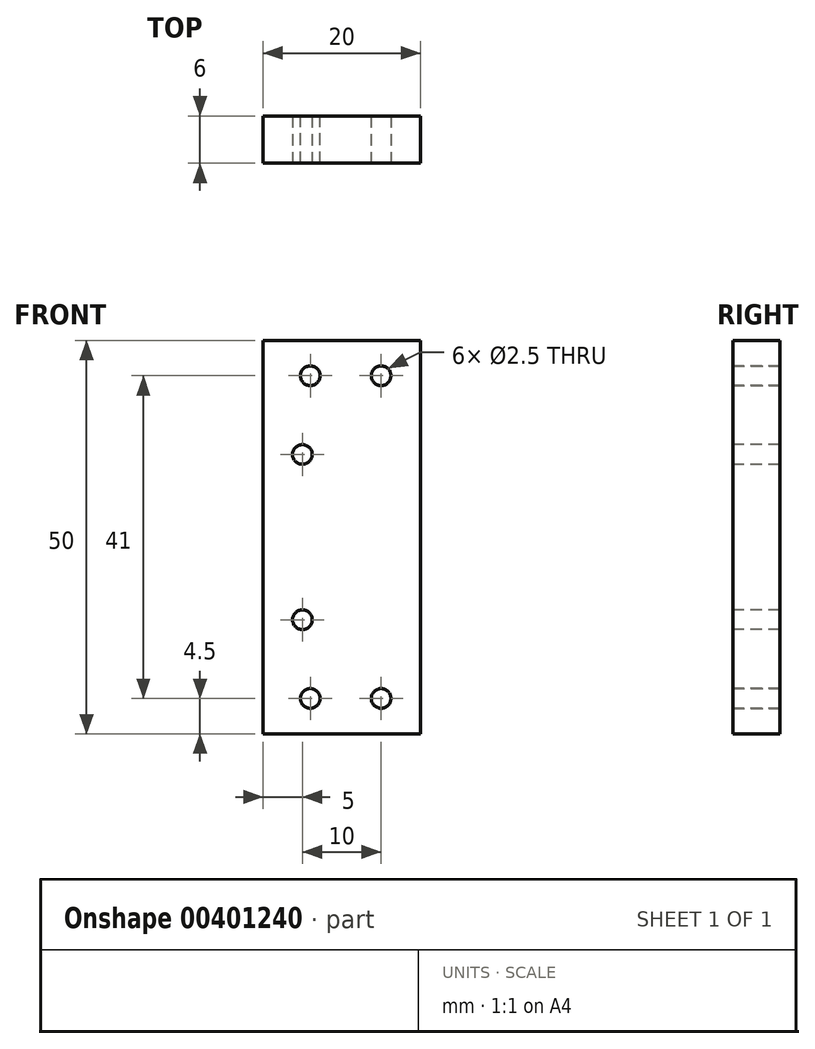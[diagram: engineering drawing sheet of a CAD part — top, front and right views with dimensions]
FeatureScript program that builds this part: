
annotation { "Feature Type Name" : "Feature", "Feature Type Description" : "" }
export const myFeature = defineFeature(function(context is Context, id is Id, definition is map)
    precondition{}
    {
        {
            var Q0;
            Q0=qCreatedBy(makeId("Front.planeOp"),FACE);
            var sketch = newSketch(context, id + "F0", { "sketchPlane" : qUnion([Q0])});
            skLineSegment(sketch, "E0.bottom", {"start": v(0, 0) * mm, "end": v(-20, 0) * mm});
            skLineSegment(sketch, "E0.top", {"start": v(0, 50) * mm, "end": v(-20, 50) * mm});
            skLineSegment(sketch, "E0.left", {"start": v(0, 0) * mm, "end": v(0, 50) * mm});
            skLineSegment(sketch, "E0.right", {"start": v(-20, 0) * mm, "end": v(-20, 50) * mm});
            skSolve(sketch);
        }
        {
            var Q0;
            Q0 = qSketchRegion(id + "F0", true);
            var Q1;
            Q1=makeQuery(id+"F0.imprint","IMPRINT",FACE,{"disambiguationData":[TD([[makeQuery(id+"F0.imprint","IMPRINT",EDGE,{"derivedFrom":sQuery(id+"F0.wireOp",EDGE,"E0.bottom")}),-1.0]])]});
            extrude(context, id + "F1", {"entities" : qUnion([Q0, Q1]), "depth" : 6 * mm});
        }
        {
            var Q0;
            Q0=makeQuery(id+"F1.opExtrude","CAP_FACE",FACE,{"disambiguationData":[OSD([sQuery(id+"F0.wireOp",EDGE,"E0.bottom"),sQuery(id+"F0.wireOp",EDGE,"E0.top"),sQuery(id+"F0.wireOp",EDGE,"E0.left"),sQuery(id+"F0.wireOp",EDGE,"E0.right")])],"isStart":false});
            var sketch = newSketch(context, id + "F2", { "sketchPlane" : qUnion([Q0])});
            skPoint(sketch, "E1", {"position": v(-15, 35.5) * mm});
            skPoint(sketch, "E2", {"position": v(-15, 14.5) * mm});
            skPoint(sketch, "E3", {"position": v(-5, 45.5) * mm});
            skPoint(sketch, "E4", {"position": v(-5, 4.5) * mm});
            skSolve(sketch);
        }
        {
            var Q0;
            Q0=sQuery(id+"F2.wireOp",VERTEX,"E3");
            var Q1;
            Q1=sQuery(id+"F2.wireOp",VERTEX,"E4");
            var Q2;
            Q2=sQuery(id+"F2.wireOp",VERTEX,"E2");
            var Q3;
            Q3=sQuery(id+"F2.wireOp",VERTEX,"E1");
            var Q4;
            Q4=makeQuery(id+"F1.opExtrude","SWEPT_BODY",BODY,{"disambiguationData":[OSD([sQuery(id+"F0.wireOp",EDGE,"E0.bottom"),sQuery(id+"F0.wireOp",EDGE,"E0.top"),sQuery(id+"F0.wireOp",EDGE,"E0.left"),sQuery(id+"F0.wireOp",EDGE,"E0.right")])]});
            hole(context, id + "F3", {"style" : HoleStyle.SIMPLE, "endStyle" : HoleEndStyle.THROUGH, "standardTappedOrClearance" : lookupTablePath({ "standard" : "ISO", "engagement" : "75%", "pitch" : "0.5 mm", "size" : "M3", "type" : "Tapped" }), "standardBlindInLast" : lookupTablePath({ "standard" : "ISO", "engagement" : "75%", "pitch" : "0.5 mm", "size" : "M3", "type" : "Tapped" }), "holeDiameter" : 2.5 * mm, "showTappedDepth" : true, "isTappedThrough" : true, "tappedDepth" : 50 * mm, "tapClearance" : 3, "startFromSketch" : true, "locations" : qUnion([Q0, Q1, Q2, Q3]), "scope" : qUnion([Q4]), "majorDiameter" : 3 * mm});
        }
        {
            var Q0;
            Q0=qCreatedBy(makeId("Front.planeOp"),FACE);
            var sketch = newSketch(context, id + "F4", { "sketchPlane" : qUnion([Q0])});
            skPoint(sketch, "E5", {"position": v(-14, 45.5) * mm});
            skPoint(sketch, "E6", {"position": v(-14, 4.5) * mm});
            skSolve(sketch);
        }
        {
            var Q0;
            Q0=sQuery(id+"F4.wireOp",VERTEX,"E5");
            var Q1;
            Q1=sQuery(id+"F4.wireOp",VERTEX,"E6");
            var Q2;
            Q2=makeQuery(id+"F1.opExtrude","SWEPT_BODY",BODY,{"disambiguationData":[OSD([sQuery(id+"F0.wireOp",EDGE,"E0.bottom"),sQuery(id+"F0.wireOp",EDGE,"E0.top"),sQuery(id+"F0.wireOp",EDGE,"E0.left"),sQuery(id+"F0.wireOp",EDGE,"E0.right")])]});
            hole(context, id + "F5", {"style" : HoleStyle.SIMPLE, "endStyle" : HoleEndStyle.THROUGH, "oppositeDirection" : true, "standardTappedOrClearance" : lookupTablePath({ "standard" : "ISO", "engagement" : "75%", "pitch" : "0.5 mm", "size" : "M3", "type" : "Tapped" }), "standardBlindInLast" : lookupTablePath({ "standard" : "ISO", "engagement" : "75%", "pitch" : "0.5 mm", "size" : "M3", "type" : "Tapped" }), "holeDiameter" : 2.5 * mm, "showTappedDepth" : true, "isTappedThrough" : true, "tappedDepth" : 50 * mm, "tapClearance" : 3, "startFromSketch" : true, "locations" : qUnion([Q0, Q1]), "scope" : qUnion([Q2]), "majorDiameter" : 3 * mm});
        }
    });
